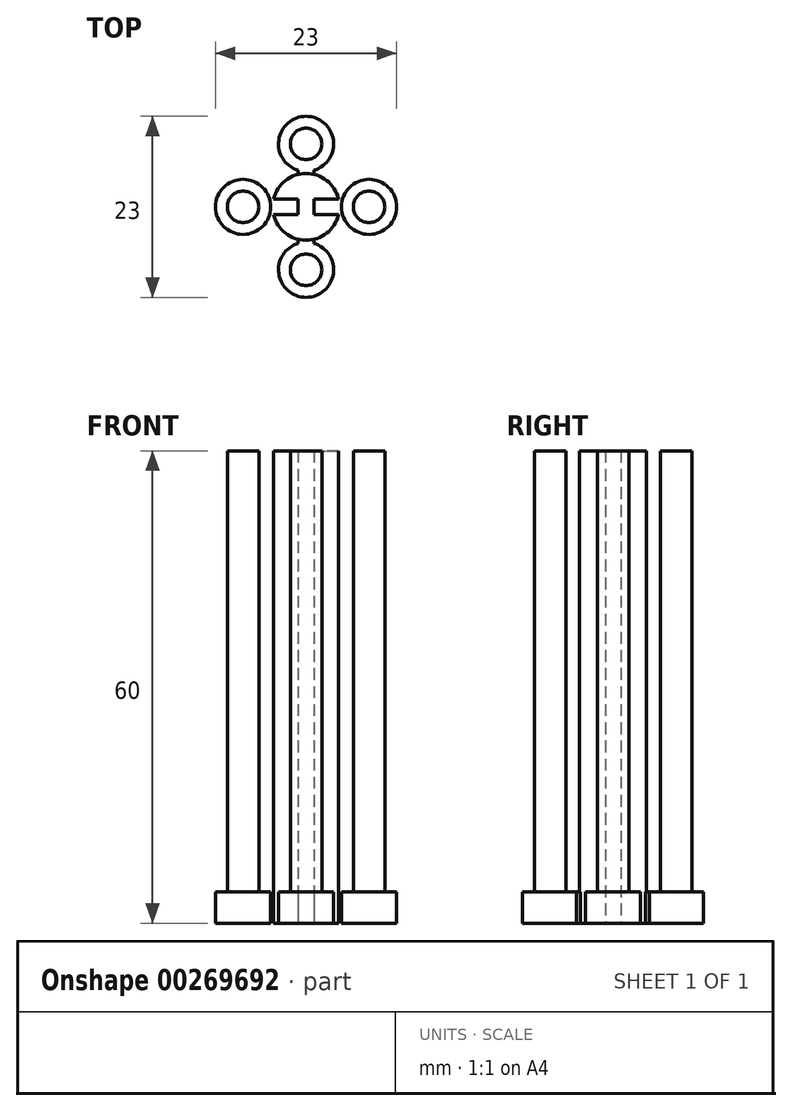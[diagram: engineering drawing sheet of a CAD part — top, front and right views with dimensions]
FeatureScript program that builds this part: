
annotation { "Feature Type Name" : "Feature", "Feature Type Description" : "" }
export const myFeature = defineFeature(function(context is Context, id is Id, definition is map)
    precondition{}
    {
        {
            var Q0;
            Q0=qCreatedBy(makeId("Top.planeOp"),FACE);
            var sketch = newSketch(context, id + "F0", { "sketchPlane" : qUnion([Q0])});
            skCircle(sketch, "E0", {"center": v(0, 0) * mm, "radius": 4.25 * mm});
            skCircle(sketch, "E1", {"center": v(0, 8) * mm, "radius": 2 * mm});
            skCircle(sketch, "E2", {"center": v(0, 8) * mm, "radius": 3.5 * mm});
            skCircle(sketch, "E3.1.0", {"center": v(-8, 0) * mm, "radius": 2 * mm});
            skCircle(sketch, "E3.1.1", {"center": v(-8, 0) * mm, "radius": 3.5 * mm});
            skCircle(sketch, "E3.2.0", {"center": v(0, -8) * mm, "radius": 2 * mm});
            skCircle(sketch, "E3.2.1", {"center": v(0, -8) * mm, "radius": 3.5 * mm});
            skCircle(sketch, "E3.3.0", {"center": v(8, 0) * mm, "radius": 2 * mm});
            skCircle(sketch, "E3.3.1", {"center": v(8, 0) * mm, "radius": 3.5 * mm});
            skLineSegment(sketch, "E4", {"start": v(-1, 4.65) * mm, "end": v(-1, -4.65) * mm});
            skLineSegment(sketch, "E5.MirrorCS", {"start": v(1, 4.65) * mm, "end": v(1, -4.65) * mm});
            skLineSegment(sketch, "E6", {"start": v(-4.65, 1) * mm, "end": v(4.65, 1) * mm});
            skLineSegment(sketch, "E7.MirrorCS", {"start": v(-4.65, -1) * mm, "end": v(4.65, -1) * mm});
            skSolve(sketch);
        }
        {
            var Q0;
            Q0=makeQuery(id+"F0.imprint","IMPRINT",FACE,{"disambiguationData":[TD([[makeQuery(id+"F0.imprint","IMPRINT",EDGE,{"derivedFrom":sQuery(id+"F0.wireOp",EDGE,"E3.1.0")}),-1.0]])]});
            var Q1;
            Q1=makeQuery(id+"F0.imprint","IMPRINT",FACE,{"disambiguationData":[TD([[makeQuery(id+"F0.imprint","IMPRINT",EDGE,{"derivedFrom":sQuery(id+"F0.wireOp",EDGE,"E3.1.0")}),1.0]])]});
            var Q2;
            Q2=makeQuery(id+"F0.imprint","IMPRINT",FACE,{"disambiguationData":[TD([[makeQuery(id+"F0.imprint","IMPRINT",EDGE,{"derivedFrom":sQuery(id+"F0.wireOp",EDGE,"E1")}),-1.0]])]});
            var Q3;
            Q3=makeQuery(id+"F0.imprint","IMPRINT",FACE,{"disambiguationData":[TD([[makeQuery(id+"F0.imprint","IMPRINT",EDGE,{"derivedFrom":sQuery(id+"F0.wireOp",EDGE,"E1")}),1.0]])]});
            var Q4;
            Q4=makeQuery(id+"F0.imprint","IMPRINT",FACE,{"disambiguationData":[TD([[makeQuery(id+"F0.imprint","IMPRINT",EDGE,{"derivedFrom":sQuery(id+"F0.wireOp",EDGE,"E3.3.0")}),1.0]])]});
            var Q5;
            Q5=makeQuery(id+"F0.imprint","IMPRINT",FACE,{"disambiguationData":[TD([[makeQuery(id+"F0.imprint","IMPRINT",EDGE,{"derivedFrom":sQuery(id+"F0.wireOp",EDGE,"E3.3.0")}),-1.0]])]});
            var Q6;
            Q6=makeQuery(id+"F0.imprint","IMPRINT",FACE,{"disambiguationData":[TD([[makeQuery(id+"F0.imprint","IMPRINT",EDGE,{"derivedFrom":sQuery(id+"F0.wireOp",EDGE,"E3.2.0")}),-1.0]])]});
            var Q7;
            Q7=makeQuery(id+"F0.imprint","IMPRINT",FACE,{"disambiguationData":[TD([[makeQuery(id+"F0.imprint","IMPRINT",EDGE,{"derivedFrom":sQuery(id+"F0.wireOp",EDGE,"E3.2.0")}),1.0]])]});
            var Q8;
            {var subQ0=sQuery(id+"F0.wireOp",EDGE,"E6");var subQ1=sQuery(id+"F0.wireOp",EDGE,"E0");var subQ2=makeQuery(id+"F0.imprint","INTERSECT",VERTEX,{"disambiguationData":[OD(1.0)],"derivedFrom":[subQ1,subQ0]});Q8=makeQuery(id+"F0.imprint","IMPRINT",FACE,{"disambiguationData":[TD([[makeQuery(id+"F0.imprint","IMPRINT",EDGE,{"disambiguationData":[TD([[subQ2,-1.0]])],"derivedFrom":subQ1}),-1.0]])]});}
            var Q9;
            {var subQ0=sQuery(id+"F0.wireOp",EDGE,"E6");var subQ1=sQuery(id+"F0.wireOp",EDGE,"E0");var subQ2=makeQuery(id+"F0.imprint","INTERSECT",VERTEX,{"disambiguationData":[OD(0.0)],"derivedFrom":[subQ1,subQ0]});Q9=makeQuery(id+"F0.imprint","IMPRINT",FACE,{"disambiguationData":[TD([[makeQuery(id+"F0.imprint","IMPRINT",EDGE,{"disambiguationData":[TD([[subQ2,1.0]])],"derivedFrom":subQ1}),-1.0]])]});}
            var Q10;
            {var subQ0=sQuery(id+"F0.wireOp",EDGE,"E4");var subQ1=sQuery(id+"F0.wireOp",EDGE,"E0");var subQ2=makeQuery(id+"F0.imprint","INTERSECT",VERTEX,{"disambiguationData":[OD(1.0)],"derivedFrom":[subQ1,subQ0]});Q10=makeQuery(id+"F0.imprint","IMPRINT",FACE,{"disambiguationData":[TD([[makeQuery(id+"F0.imprint","IMPRINT",EDGE,{"disambiguationData":[TD([[subQ2,-1.0]])],"derivedFrom":subQ1}),-1.0]])]});}
            var Q11;
            {var subQ0=sQuery(id+"F0.wireOp",EDGE,"E5.MirrorCS");var subQ1=sQuery(id+"F0.wireOp",EDGE,"E0");var subQ2=makeQuery(id+"F0.imprint","INTERSECT",VERTEX,{"disambiguationData":[OD(0.0)],"derivedFrom":[subQ1,subQ0]});Q11=makeQuery(id+"F0.imprint","IMPRINT",FACE,{"disambiguationData":[TD([[makeQuery(id+"F0.imprint","IMPRINT",EDGE,{"disambiguationData":[TD([[subQ2,-1.0]])],"derivedFrom":subQ1}),-1.0]])]});}
            var Q12;
            {var subQ0=sQuery(id+"F0.wireOp",EDGE,"E5.MirrorCS");var subQ1=sQuery(id+"F0.wireOp",EDGE,"E0");var subQ2=makeQuery(id+"F0.imprint","INTERSECT",VERTEX,{"disambiguationData":[OD(0.0)],"derivedFrom":[subQ1,subQ0]});Q12=makeQuery(id+"F0.imprint","IMPRINT",FACE,{"disambiguationData":[TD([[makeQuery(id+"F0.imprint","IMPRINT",EDGE,{"disambiguationData":[TD([[subQ2,-1.0]])],"derivedFrom":subQ1}),1.0]])]});}
            var Q13;
            {var subQ0=sQuery(id+"F0.wireOp",EDGE,"E4");var subQ1=sQuery(id+"F0.wireOp",EDGE,"E0");var subQ2=makeQuery(id+"F0.imprint","INTERSECT",VERTEX,{"disambiguationData":[OD(1.0)],"derivedFrom":[subQ1,subQ0]});Q13=makeQuery(id+"F0.imprint","IMPRINT",FACE,{"disambiguationData":[TD([[makeQuery(id+"F0.imprint","IMPRINT",EDGE,{"disambiguationData":[TD([[subQ2,-1.0]])],"derivedFrom":subQ1}),1.0]])]});}
            var Q14;
            {var subQ0=sQuery(id+"F0.wireOp",EDGE,"E6");var subQ1=sQuery(id+"F0.wireOp",EDGE,"E4");var subQ2=makeQuery(id+"F0.imprint","INTERSECT",VERTEX,{"derivedFrom":[subQ1,subQ0]});Q14=makeQuery(id+"F0.imprint","IMPRINT",FACE,{"disambiguationData":[TD([[makeQuery(id+"F0.imprint","IMPRINT",EDGE,{"disambiguationData":[TD([[subQ2,-1.0]])],"derivedFrom":subQ1}),1.0]])]});}
            var Q15;
            {var subQ0=sQuery(id+"F0.wireOp",EDGE,"E6");var subQ1=sQuery(id+"F0.wireOp",EDGE,"E0");var subQ2=makeQuery(id+"F0.imprint","INTERSECT",VERTEX,{"disambiguationData":[OD(0.0)],"derivedFrom":[subQ1,subQ0]});Q15=makeQuery(id+"F0.imprint","IMPRINT",FACE,{"disambiguationData":[TD([[makeQuery(id+"F0.imprint","IMPRINT",EDGE,{"disambiguationData":[TD([[subQ2,1.0]])],"derivedFrom":subQ1}),1.0]])]});}
            var Q16;
            {var subQ0=sQuery(id+"F0.wireOp",EDGE,"E6");var subQ1=sQuery(id+"F0.wireOp",EDGE,"E0");var subQ2=makeQuery(id+"F0.imprint","INTERSECT",VERTEX,{"disambiguationData":[OD(1.0)],"derivedFrom":[subQ1,subQ0]});Q16=makeQuery(id+"F0.imprint","IMPRINT",FACE,{"disambiguationData":[TD([[makeQuery(id+"F0.imprint","IMPRINT",EDGE,{"disambiguationData":[TD([[subQ2,-1.0]])],"derivedFrom":subQ1}),1.0]])]});}
            extrude(context, id + "F1", {"entities" : qUnion([Q0, Q1, Q2, Q3, Q4, Q5, Q6, Q7, Q8, Q9, Q10, Q11, Q12, Q13, Q14, Q15, Q16]), "depth" : 4 * mm});
        }
        {
            var Q0;
            Q0=makeQuery(id+"F0.imprint","IMPRINT",FACE,{"disambiguationData":[TD([[makeQuery(id+"F0.imprint","IMPRINT",EDGE,{"derivedFrom":sQuery(id+"F0.wireOp",EDGE,"E1")}),1.0]])]});
            var Q1;
            Q1=makeQuery(id+"F0.imprint","IMPRINT",FACE,{"disambiguationData":[TD([[makeQuery(id+"F0.imprint","IMPRINT",EDGE,{"derivedFrom":sQuery(id+"F0.wireOp",EDGE,"E3.3.0")}),1.0]])]});
            var Q2;
            Q2=makeQuery(id+"F0.imprint","IMPRINT",FACE,{"disambiguationData":[TD([[makeQuery(id+"F0.imprint","IMPRINT",EDGE,{"derivedFrom":sQuery(id+"F0.wireOp",EDGE,"E3.1.0")}),1.0]])]});
            var Q3;
            Q3=makeQuery(id+"F0.imprint","IMPRINT",FACE,{"disambiguationData":[TD([[makeQuery(id+"F0.imprint","IMPRINT",EDGE,{"derivedFrom":sQuery(id+"F0.wireOp",EDGE,"E3.2.0")}),1.0]])]});
            var Q4;
            {var subQ0=sQuery(id+"F0.wireOp",EDGE,"E7.MirrorCS");var subQ1=sQuery(id+"F0.wireOp",EDGE,"E0");var subQ2=makeQuery(id+"F0.imprint","INTERSECT",VERTEX,{"disambiguationData":[OD(0.0)],"derivedFrom":[subQ1,subQ0]});Q4=makeQuery(id+"F0.imprint","IMPRINT",FACE,{"disambiguationData":[TD([[makeQuery(id+"F0.imprint","IMPRINT",EDGE,{"disambiguationData":[TD([[subQ2,-1.0]])],"derivedFrom":subQ1}),1.0]])]});}
            var Q5;
            {var subQ0=sQuery(id+"F0.wireOp",EDGE,"E5.MirrorCS");var subQ1=sQuery(id+"F0.wireOp",EDGE,"E0");var subQ2=makeQuery(id+"F0.imprint","INTERSECT",VERTEX,{"disambiguationData":[OD(1.0)],"derivedFrom":[subQ1,subQ0]});Q5=makeQuery(id+"F0.imprint","IMPRINT",FACE,{"disambiguationData":[TD([[makeQuery(id+"F0.imprint","IMPRINT",EDGE,{"disambiguationData":[TD([[subQ2,-1.0]])],"derivedFrom":subQ1}),1.0]])]});}
            var Q6;
            {var subQ0=sQuery(id+"F0.wireOp",EDGE,"E5.MirrorCS");var subQ1=sQuery(id+"F0.wireOp",EDGE,"E0");var subQ2=makeQuery(id+"F0.imprint","INTERSECT",VERTEX,{"disambiguationData":[OD(0.0)],"derivedFrom":[subQ1,subQ0]});Q6=makeQuery(id+"F0.imprint","IMPRINT",FACE,{"disambiguationData":[TD([[makeQuery(id+"F0.imprint","IMPRINT",EDGE,{"disambiguationData":[TD([[subQ2,1.0]])],"derivedFrom":subQ1}),1.0]])]});}
            var Q7;
            {var subQ0=sQuery(id+"F0.wireOp",EDGE,"E4");var subQ1=sQuery(id+"F0.wireOp",EDGE,"E0");var subQ2=makeQuery(id+"F0.imprint","INTERSECT",VERTEX,{"disambiguationData":[OD(0.0)],"derivedFrom":[subQ1,subQ0]});Q7=makeQuery(id+"F0.imprint","IMPRINT",FACE,{"disambiguationData":[TD([[makeQuery(id+"F0.imprint","IMPRINT",EDGE,{"disambiguationData":[TD([[subQ2,-1.0]])],"derivedFrom":subQ1}),1.0]])]});}
            var Q8;
            {var subQ0=sQuery(id+"F0.wireOp",EDGE,"E5.MirrorCS");var subQ1=sQuery(id+"F0.wireOp",EDGE,"E0");var subQ2=makeQuery(id+"F0.imprint","INTERSECT",VERTEX,{"disambiguationData":[OD(0.0)],"derivedFrom":[subQ1,subQ0]});Q8=makeQuery(id+"F0.imprint","IMPRINT",FACE,{"disambiguationData":[TD([[makeQuery(id+"F0.imprint","IMPRINT",EDGE,{"disambiguationData":[TD([[subQ2,-1.0]])],"derivedFrom":subQ1}),1.0]])]});}
            var Q9;
            {var subQ0=sQuery(id+"F0.wireOp",EDGE,"E6");var subQ1=sQuery(id+"F0.wireOp",EDGE,"E0");var subQ2=makeQuery(id+"F0.imprint","INTERSECT",VERTEX,{"disambiguationData":[OD(1.0)],"derivedFrom":[subQ1,subQ0]});Q9=makeQuery(id+"F0.imprint","IMPRINT",FACE,{"disambiguationData":[TD([[makeQuery(id+"F0.imprint","IMPRINT",EDGE,{"disambiguationData":[TD([[subQ2,-1.0]])],"derivedFrom":subQ1}),1.0]])]});}
            var Q10;
            {var subQ0=sQuery(id+"F0.wireOp",EDGE,"E4");var subQ1=sQuery(id+"F0.wireOp",EDGE,"E0");var subQ2=makeQuery(id+"F0.imprint","INTERSECT",VERTEX,{"disambiguationData":[OD(1.0)],"derivedFrom":[subQ1,subQ0]});Q10=makeQuery(id+"F0.imprint","IMPRINT",FACE,{"disambiguationData":[TD([[makeQuery(id+"F0.imprint","IMPRINT",EDGE,{"disambiguationData":[TD([[subQ2,-1.0]])],"derivedFrom":subQ1}),1.0]])]});}
            var Q11;
            {var subQ0=sQuery(id+"F0.wireOp",EDGE,"E6");var subQ1=sQuery(id+"F0.wireOp",EDGE,"E4");var subQ2=makeQuery(id+"F0.imprint","INTERSECT",VERTEX,{"derivedFrom":[subQ1,subQ0]});Q11=makeQuery(id+"F0.imprint","IMPRINT",FACE,{"disambiguationData":[TD([[makeQuery(id+"F0.imprint","IMPRINT",EDGE,{"disambiguationData":[TD([[subQ2,-1.0]])],"derivedFrom":subQ1}),1.0]])]});}
            var Q12;
            {var subQ0=sQuery(id+"F0.wireOp",EDGE,"E6");var subQ1=sQuery(id+"F0.wireOp",EDGE,"E0");var subQ2=makeQuery(id+"F0.imprint","INTERSECT",VERTEX,{"disambiguationData":[OD(0.0)],"derivedFrom":[subQ1,subQ0]});Q12=makeQuery(id+"F0.imprint","IMPRINT",FACE,{"disambiguationData":[TD([[makeQuery(id+"F0.imprint","IMPRINT",EDGE,{"disambiguationData":[TD([[subQ2,1.0]])],"derivedFrom":subQ1}),1.0]])]});}
            extrude(context, id + "F2", {"entities" : qUnion([Q0, Q1, Q2, Q3, Q4, Q5, Q6, Q7, Q8, Q9, Q10, Q11, Q12]), "operationType" : NewBodyOperationType.ADD, "depth" : 60 * mm});
        }
    });
